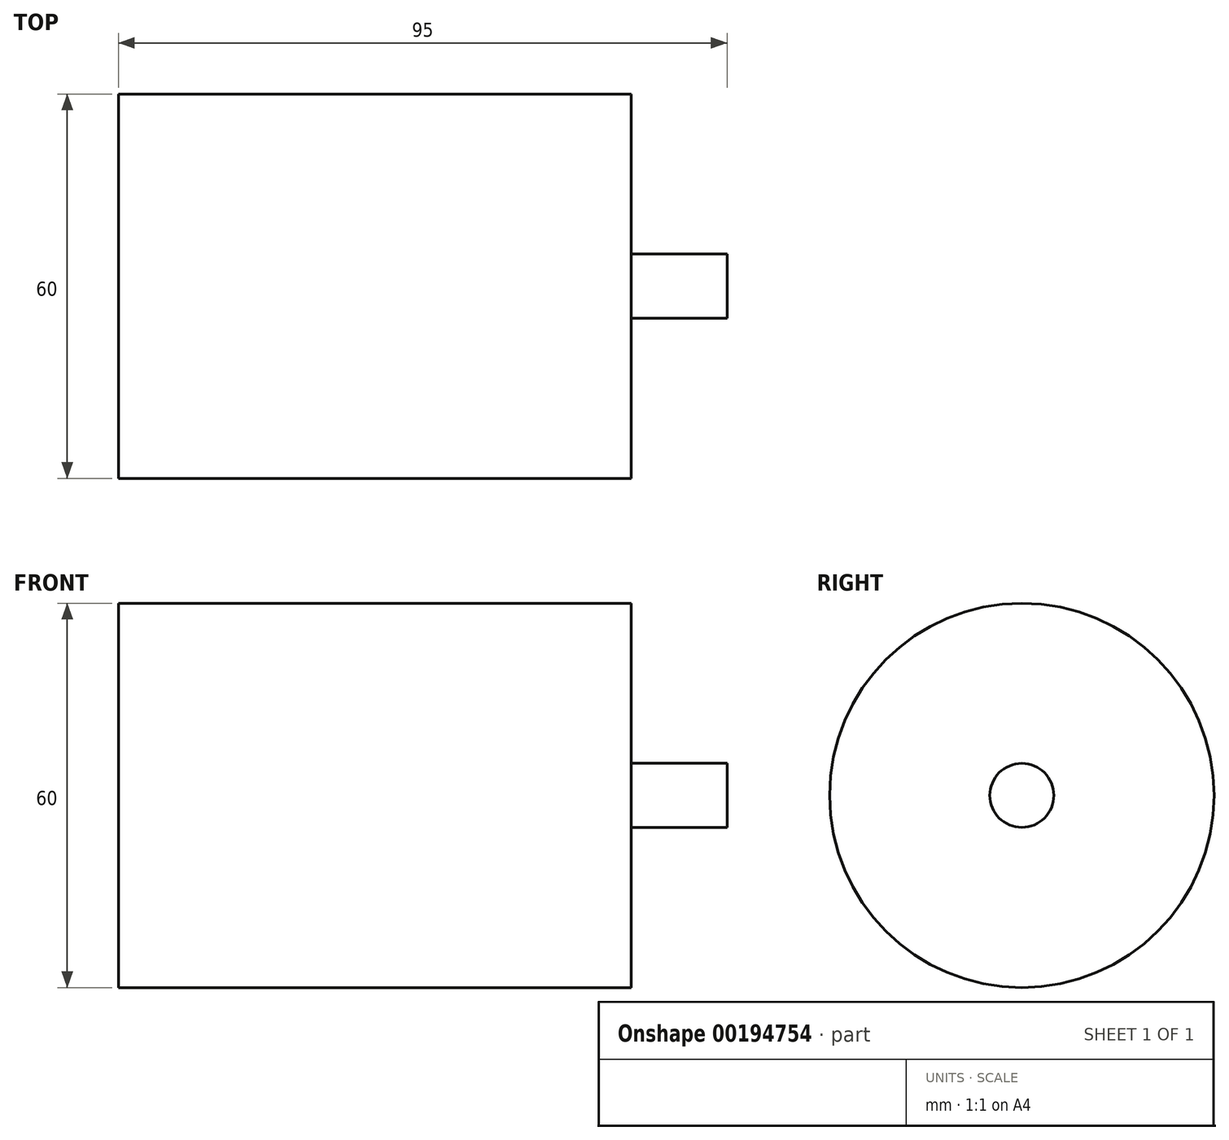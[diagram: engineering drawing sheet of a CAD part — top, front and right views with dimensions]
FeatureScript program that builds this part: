
annotation { "Feature Type Name" : "Feature", "Feature Type Description" : "" }
export const myFeature = defineFeature(function(context is Context, id is Id, definition is map)
    precondition{}
    {
        {
            var Q0;
            Q0=qCreatedBy(makeId("Front.planeOp"),FACE);
            var sketch = newSketch(context, id + "F0", { "sketchPlane" : qUnion([Q0])});
            skLineSegment(sketch, "E0.top", {"start": v(-64.89, 30) * mm, "end": v(15.11, 30) * mm});
            skLineSegment(sketch, "E0.left", {"start": v(-64.89, 0) * mm, "end": v(-64.89, 30) * mm});
            skLineSegment(sketch, "E0.right", {"start": v(15.11, 5) * mm, "end": v(15.11, 30) * mm});
            skLineSegment(sketch, "E1.bottom", {"start": v(15.11, 5) * mm, "end": v(30.11, 5) * mm});
            skLineSegment(sketch, "E1.top", {"start": v(-64.89, 0) * mm, "end": v(30.11, 0) * mm});
            skLineSegment(sketch, "E1.right", {"start": v(30.11, 5) * mm, "end": v(30.11, 0) * mm});
            skLineSegment(sketch, "E2", {"start": v(-71.44, 0) * mm, "end": v(65.67, 0) * mm, "construction": true});
            skPoint(sketch, "E2.endSnap0", {"position": v(-17.39, 0) * mm});
            skSolve(sketch);
        }
        {
            var Q0;
            Q0=makeQuery(id+"F0.imprint","IMPRINT",FACE,{"disambiguationData":[TD([[makeQuery(id+"F0.imprint","IMPRINT",EDGE,{"derivedFrom":sQuery(id+"F0.wireOp",EDGE,"E0.top")}),-1.0]])]});
            var Q1;
            Q1=sQuery(id+"F0.wireOp",EDGE,"E2");
            revolve(context, id + "F1", {"entities" : qUnion([Q0]), "axis" : qUnion([Q1]), "revolveType" : RevolveType.FULL});
        }
    });
